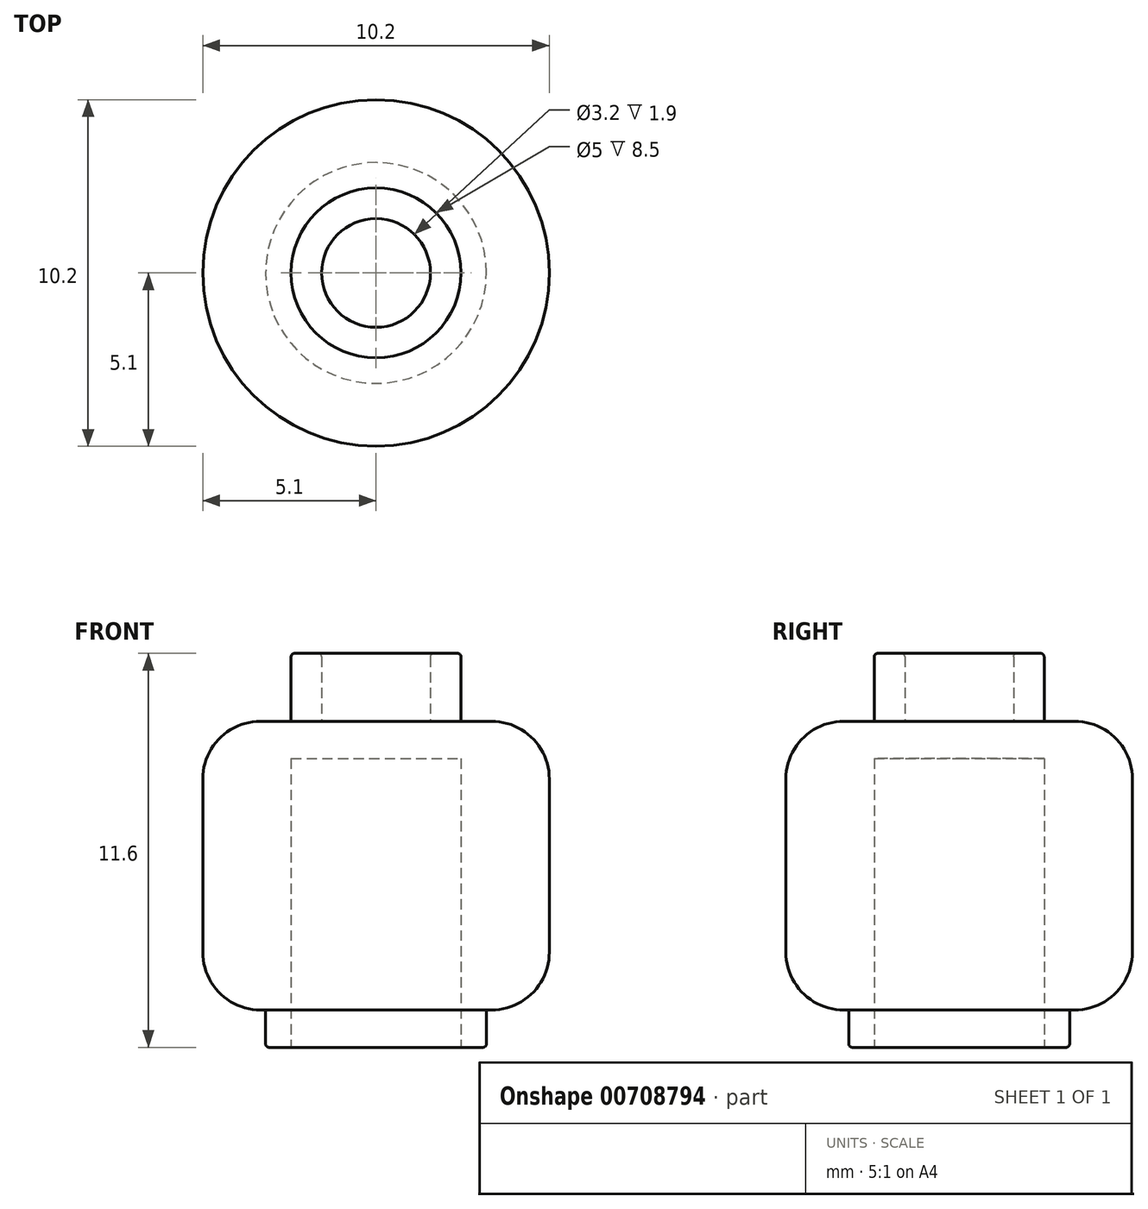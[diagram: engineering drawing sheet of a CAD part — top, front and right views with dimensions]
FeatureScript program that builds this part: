
annotation { "Feature Type Name" : "Feature", "Feature Type Description" : "" }
export const myFeature = defineFeature(function(context is Context, id is Id, definition is map)
    precondition{}
    {
        {
            var Q0;
            Q0=qCreatedBy(makeId("Top.planeOp"),FACE);
            var sketch = newSketch(context, id + "F0", { "sketchPlane" : qUnion([Q0])});
            skCircle(sketch, "E0", {"center": v(0, 0) * mm, "radius": 3.25 * mm});
            skSolve(sketch);
        }
        {
            var Q0;
            Q0=makeQuery(id+"F0.imprint","IMPRINT",FACE,{"disambiguationData":[TD([[makeQuery(id+"F0.imprint","IMPRINT",EDGE,{"derivedFrom":sQuery(id+"F0.wireOp",EDGE,"E0")}),1.0]])]});
            extrude(context, id + "F1", {"entities" : qUnion([Q0]), "depth" : 1.1 * mm});
        }
        {
            var Q0;
            Q0=makeQuery(id+"F1.opExtrude","CAP_FACE",FACE,{"disambiguationData":[OSD([sQuery(id+"F0.wireOp",EDGE,"E0")])],"isStart":false});
            var sketch = newSketch(context, id + "F2", { "sketchPlane" : qUnion([Q0])});
            skCircle(sketch, "E1", {"center": v(0, 0) * mm, "radius": 5.1 * mm});
            skSolve(sketch);
        }
        {
            var Q0;
            Q0=qSketchRegion(id+"F2",true);
            extrude(context, id + "F3", {"entities" : qUnion([Q0]), "operationType" : NewBodyOperationType.ADD, "depth" : 8.5 * mm});
        }
        {
            var Q0;
            Q0=makeQuery(id+"F3.opExtrude","CAP_FACE",FACE,{"disambiguationData":[OSD([sQuery(id+"F2.wireOp",EDGE,"E1")])],"isStart":false});
            var sketch = newSketch(context, id + "F4", { "sketchPlane" : qUnion([Q0])});
            skCircle(sketch, "E2", {"center": v(0, 0) * mm, "radius": 2.5 * mm});
            skCircle(sketch, "E3", {"center": v(0, 0) * mm, "radius": 1.6 * mm});
            skSolve(sketch);
        }
        {
            var Q0;
            Q0=qSketchRegion(id+"F4",true);
            extrude(context, id + "F5", {"entities" : qUnion([Q0]), "operationType" : NewBodyOperationType.ADD, "depth" : 2 * mm});
        }
        {
            var Q0;
            Q0=makeQuery(id+"F1.opExtrude","CAP_FACE",FACE,{"disambiguationData":[OSD([sQuery(id+"F0.wireOp",EDGE,"E0")])],"isStart":true});
            var sketch = newSketch(context, id + "F6", { "sketchPlane" : qUnion([Q0])});
            skCircle(sketch, "E4", {"center": v(0, 0) * mm, "radius": 2.5 * mm});
            skSolve(sketch);
        }
        {
            var Q0;
            Q0=qSketchRegion(id+"F6",true);
            var Q1;
            Q1=makeQuery(id+"F6.imprint","IMPRINT",FACE,{"disambiguationData":[TD([[makeQuery(id+"F6.imprint","IMPRINT",EDGE,{"derivedFrom":sQuery(id+"F6.wireOp",EDGE,"E4")}),1.0]])]});
            extrude(context, id + "F7", {"entities" : qUnion([Q0, Q1]), "operationType" : NewBodyOperationType.REMOVE, "oppositeDirection" : true, "depth" : 8.5 * mm});
        }
        {
            var Q0;
            Q0=makeQuery(id+"F1.opExtrude","CAP_EDGE",EDGE,{"disambiguationData":[OSD([sQuery(id+"F0.wireOp",EDGE,"E0")])],"isStart":true});
            var Q1;
            Q1=makeQuery(id+"F5.opExtrude","CAP_EDGE",EDGE,{"disambiguationData":[OSD([sQuery(id+"F4.wireOp",EDGE,"E2")])],"isStart":false});
            var Q2;
            Q2=makeQuery(id+"F5.opExtrude","CAP_EDGE",EDGE,{"disambiguationData":[OSD([sQuery(id+"F4.wireOp",EDGE,"E3")])],"isStart":false});
            fillet(context, id + "F8", {"entities" : qUnion([Q0, Q1, Q2]), "radius" : 0.1 * mm, "tangentPropagation" : true, "allowEdgeOverflow" : false});
        }
        {
            var Q0;
            Q0=makeQuery(id+"F3.opExtrude","CAP_EDGE",EDGE,{"disambiguationData":[OSD([sQuery(id+"F2.wireOp",EDGE,"E1")])],"isStart":false});
            var Q1;
            Q1=makeQuery(id+"F3.opExtrude","CAP_EDGE",EDGE,{"disambiguationData":[OSD([sQuery(id+"F2.wireOp",EDGE,"E1")])],"isStart":true});
            fillet(context, id + "F9", {"entities" : qUnion([Q0, Q1]), "radius" : 1.7 * mm, "tangentPropagation" : true, "allowEdgeOverflow" : false});
        }
    });
